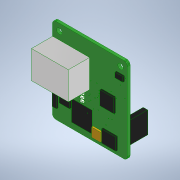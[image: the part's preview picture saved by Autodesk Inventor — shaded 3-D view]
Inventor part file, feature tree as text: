
AUTODESK INVENTOR PART (.ipt)
format: ipt  version: 2020 (Build 240168000, 168)  size: 376,832 bytes
history: native  units: in
note: dims shown in document units (in); Inventor stores cm internally (conversion verified against a paired STEP export)
features: extrude x13, other x12, sketch x1
ambient origin geometry x8: Origin, YZ Plane, XZ Plane, XY Plane, X Axis, Y Axis, Z Axis, Center Point
bodies: Solid1 (feature_tree)
feature tree (26):
  other  "ethernet_poe.brd"
  extrude  "ethernet_poe.brd_Outline"  Depth=0.063in
  extrude  "C20_2"  Depth=0.0394in TaperAngle=0.0deg
  extrude  "D2_4"  Depth=0.0394in TaperAngle=0.0deg
  extrude  "D3_6"  Depth=0.0394in TaperAngle=0.0deg
  extrude  "D4_8"  Depth=0.0394in TaperAngle=0.0deg
  extrude  "J1_10"  Depth=0.4921in TaperAngle=0.0deg
  extrude  "J2_12"  Depth=0.4961in TaperAngle=0.0deg
  extrude  "J3_14"  Depth=0.4961in TaperAngle=0.0deg
  extrude  "UH_16"  Depth=0.0004in TaperAngle=0.0deg
  extrude  "S1_18"  Depth=0.0394in TaperAngle=0.0deg
  extrude  "U1_22"  Depth=0.0394in TaperAngle=0.0deg
  extrude  "U2_24"  Depth=0.0394in TaperAngle=0.0deg
  extrude  "U3_26"  Depth=0.0394in TaperAngle=0.0deg
  sketch  "Sketch1"  dims[d0=0.063in d1=0.0in d2=0.063in d3=0.0394in d4=0.0in d5=0.0394in d6=0.0in d7=0.0394in d8=0.0in d9=0.0394in d10=0.0in d11=0.4921in d12=0.0in d13=0.4961in d14=0.0in d15=0.4961in d16=0.0in d17=0.0004in d18=0.0in d19=0.0394in d20=0.0in d23=0.0394in d24=0.0in d25=0.0394in d26=0.0in d27=0.0394in d28=0.0in]
  other  "E2-5, E2-5_1"
  other  "CHIP-LED0603, CHIP-LED0603_3"
  other  "CHIP-LED0603, CHIP-LED0603_5"
  other  "CHIP-LED0603, CHIP-LED0603_7"
  other  "ARJP11A-MBSB-A-B-EMU2, ARJP11A_9"
  other  "1X05, J2_1X05_11"
  other  "1X05, J3_1X05_13"
  other  "KMR2, KMR2_17"
  other  "48-LQFP, W5500_21"
  other  "SOIC-8-EXPOSED_PAD, IFX91041_23"
  other  "SOT230P700X180-4N, AZ1117EH-3_3TRG1_25"
